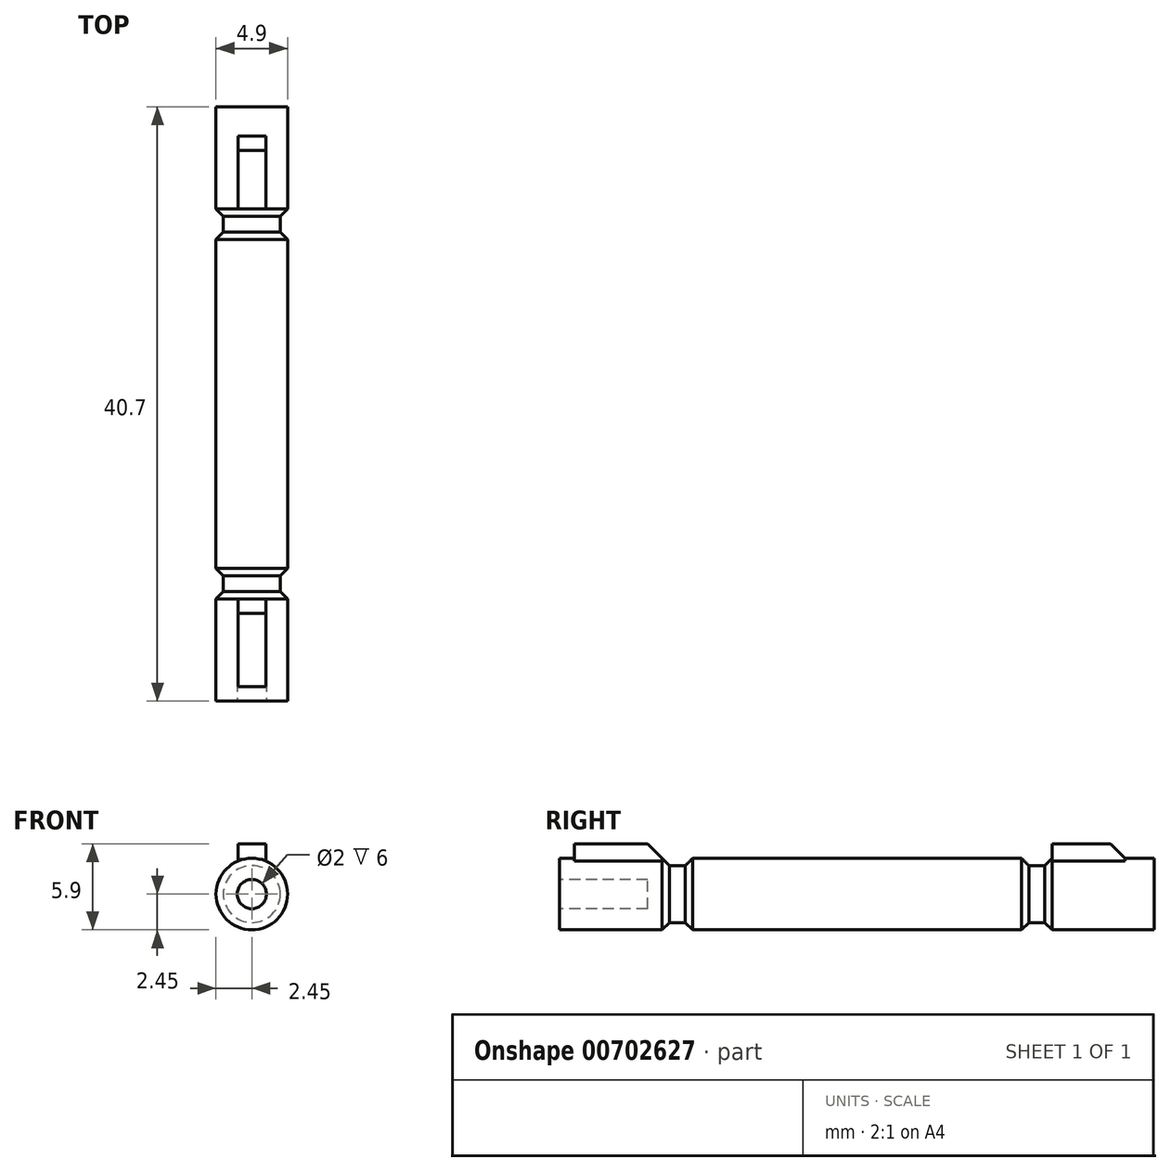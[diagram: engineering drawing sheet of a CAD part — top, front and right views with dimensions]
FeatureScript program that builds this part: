
annotation { "Feature Type Name" : "Feature", "Feature Type Description" : "" }
export const myFeature = defineFeature(function(context is Context, id is Id, definition is map)
    precondition{}
    {
        {
            var Q0;
            Q0=qCreatedBy(makeId("Top.planeOp"),FACE);
            var sketch = newSketch(context, id + "F0", { "sketchPlane" : qUnion([Q0])});
            skLineSegment(sketch, "E0", {"start": v(0, 9.66) * mm, "end": v(0, -39.97) * mm, "construction": true});
            skLineSegment(sketch, "E1", {"start": v(0, 0) * mm, "end": v(-2.45, 0) * mm});
            skLineSegment(sketch, "E2", {"start": v(-2.45, -32.1) * mm, "end": v(-1.95, -32.1) * mm});
            skLineSegment(sketch, "E3", {"start": v(-1.95, -32.1) * mm, "end": v(-1.95, -33.2) * mm});
            skLineSegment(sketch, "E4", {"start": v(-1.95, -33.2) * mm, "end": v(-2.45, -33.2) * mm});
            skLineSegment(sketch, "E5", {"start": v(-2.45, -7.5) * mm, "end": v(-1.95, -7.5) * mm});
            skLineSegment(sketch, "E6", {"start": v(-1.95, -7.5) * mm, "end": v(-1.95, -8.6) * mm});
            skLineSegment(sketch, "E7", {"start": v(-1.95, -8.6) * mm, "end": v(-2.45, -8.6) * mm});
            skLineSegment(sketch, "E8", {"start": v(-2.45, 0) * mm, "end": v(-2.45, -7.5) * mm});
            skLineSegment(sketch, "E9", {"start": v(-2.45, -8.6) * mm, "end": v(-2.45, -32.1) * mm});
            skLineSegment(sketch, "E10", {"start": v(-2.45, -33.2) * mm, "end": v(-2.45, -40.7) * mm});
            skLineSegment(sketch, "E11", {"start": v(-2.45, -40.7) * mm, "end": v(0, -40.7) * mm});
            skLineSegment(sketch, "E12", {"start": v(0, 0) * mm, "end": v(0, -40.7) * mm});
            skSolve(sketch);
        }
        {
            var Q0;
            Q0=qCreatedBy(makeId("Top.planeOp"),FACE);
            var sketch = newSketch(context, id + "F1", { "sketchPlane" : qUnion([Q0])});
            skLineSegment(sketch, "E13.bottom", {"start": v(0.95, -7) * mm, "end": v(-0.95, -7) * mm});
            skLineSegment(sketch, "E13.top", {"start": v(0.95, -2) * mm, "end": v(-0.95, -2) * mm});
            skLineSegment(sketch, "E13.left", {"start": v(0.95, -7) * mm, "end": v(0.95, -2) * mm});
            skLineSegment(sketch, "E13.right", {"start": v(-0.95, -7) * mm, "end": v(-0.95, -2) * mm});
            skPoint(sketch, "E13.middle", {"position": v(0, -4.5) * mm});
            skLineSegment(sketch, "E14.bottom", {"start": v(-0.95, -33.7) * mm, "end": v(0.95, -33.7) * mm});
            skLineSegment(sketch, "E14.top", {"start": v(-0.95, -39.7) * mm, "end": v(0.95, -39.7) * mm});
            skLineSegment(sketch, "E14.left", {"start": v(-0.95, -33.7) * mm, "end": v(-0.95, -39.7) * mm});
            skLineSegment(sketch, "E14.right", {"start": v(0.95, -33.7) * mm, "end": v(0.95, -39.7) * mm});
            skSolve(sketch);
        }
        {
            var Q0;
            Q0=makeQuery(id+"F0.imprint","IMPRINT",FACE,{"disambiguationData":[TD([[makeQuery(id+"F0.imprint","IMPRINT",EDGE,{"derivedFrom":sQuery(id+"F0.wireOp",EDGE,"E1")}),1.0]])]});
            var Q1;
            Q1=sQuery(id+"F0.wireOp",EDGE,"E0");
            revolve(context, id + "F2", {"surfaceOperationType" : NewSurfaceOperationType.NEW, "entities" : qUnion([Q0]), "axis" : qUnion([Q1]), "revolveType" : RevolveType.FULL});
        }
        {
            var Q0;
            Q0=makeQuery(id+"F2.opRevolve","SWEPT_EDGE",EDGE,{"disambiguationData":[OSD([sQuery(id+"F0.wireOp",EDGE,"E7"),sQuery(id+"F0.wireOp",EDGE,"E9")])]});
            var Q1;
            Q1=makeQuery(id+"F2.opRevolve","SWEPT_EDGE",EDGE,{"disambiguationData":[OSD([sQuery(id+"F0.wireOp",EDGE,"E4"),sQuery(id+"F0.wireOp",EDGE,"E10")])]});
            var Q2;
            Q2=makeQuery(id+"F2.opRevolve","SWEPT_EDGE",EDGE,{"disambiguationData":[OSD([sQuery(id+"F0.wireOp",EDGE,"E5"),sQuery(id+"F0.wireOp",EDGE,"E8")])]});
            var Q3;
            Q3=makeQuery(id+"F2.opRevolve","SWEPT_EDGE",EDGE,{"disambiguationData":[OSD([sQuery(id+"F0.wireOp",EDGE,"E2"),sQuery(id+"F0.wireOp",EDGE,"E9")])]});
            chamfer(context, id + "F3", {"entities" : qUnion([Q0, Q1, Q2, Q3]), "width" : 0.5 * mm, "tangentPropagation" : true});
        }
        {
            var Q0;
            Q0 = qSketchRegion(id + "F1", true);
            extrude(context, id + "F4", {"entities" : qUnion([Q0]), "operationType" : NewBodyOperationType.ADD, "depth" : 3.45 * mm, "offsetDistance" : 25 * mm});
        }
        {
            var Q0;
            Q0=makeQuery(id+"F4.opExtrude","CAP_EDGE",EDGE,{"disambiguationData":[OSD([sQuery(id+"F1.wireOp",EDGE,"E14.bottom")])],"isStart":false});
            var Q1;
            Q1=makeQuery(id+"F4.opExtrude","CAP_EDGE",EDGE,{"disambiguationData":[OSD([sQuery(id+"F1.wireOp",EDGE,"E13.top")])],"isStart":false});
            chamfer(context, id + "F5", {"entities" : qUnion([Q0, Q1]), "width" : 1 * mm, "tangentPropagation" : true});
        }
        {
            var Q0;
            Q0=makeQuery(id+"F2.opRevolve","SWEPT_FACE",FACE,{"disambiguationData":[OSD([sQuery(id+"F0.wireOp",EDGE,"E11")])]});
            var sketch = newSketch(context, id + "F6", { "sketchPlane" : qUnion([Q0])});
            skCircle(sketch, "E15", {"center": v(0, 0) * mm, "radius": 1 * mm});
            skSolve(sketch);
        }
        {
            var Q0;
            Q0=makeQuery(id+"F6.imprint","IMPRINT",FACE,{"disambiguationData":[TD([[makeQuery(id+"F6.imprint","IMPRINT",EDGE,{"derivedFrom":sQuery(id+"F6.wireOp",EDGE,"E15")}),1.0]])]});
            extrude(context, id + "F7", {"entities" : qUnion([Q0]), "operationType" : NewBodyOperationType.REMOVE, "oppositeDirection" : true, "depth" : 6 * mm, "offsetDistance" : 25 * mm});
        }
    });
